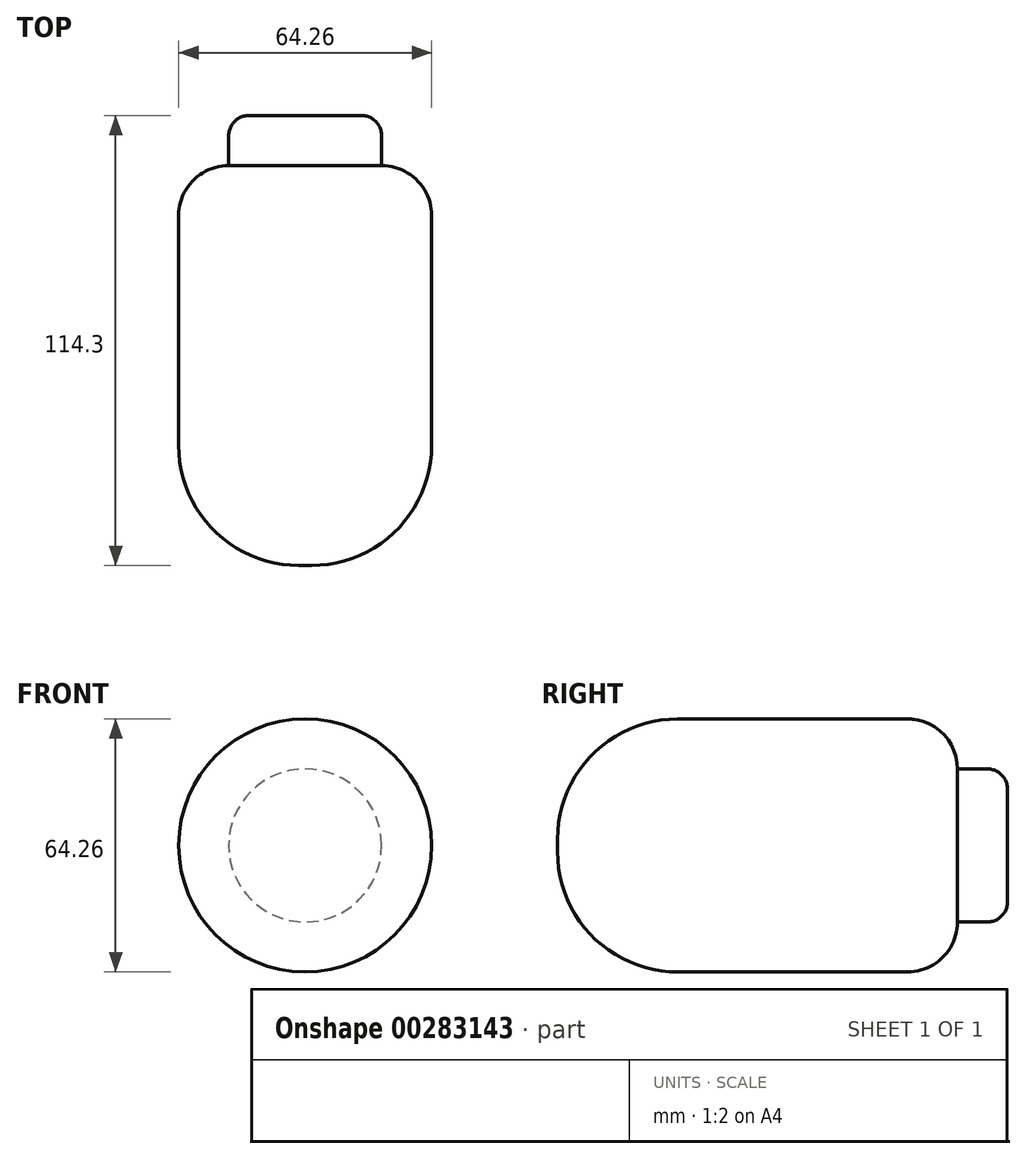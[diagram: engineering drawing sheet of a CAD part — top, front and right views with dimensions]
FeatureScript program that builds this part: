
annotation { "Feature Type Name" : "Feature", "Feature Type Description" : "" }
export const myFeature = defineFeature(function(context is Context, id is Id, definition is map)
    precondition{}
    {
        {
            var Q0;
            Q0=qCreatedBy(makeId("Front.planeOp"),FACE);
            var sketch = newSketch(context, id + "F0", { "sketchPlane" : qUnion([Q0])});
            skCircle(sketch, "E0", {"center": v(0, 0) * mm, "radius": 32.13 * mm});
            skSolve(sketch);
        }
        {
            var Q0;
            Q0=makeQuery(id+"F0.imprint","IMPRINT",FACE,{"disambiguationData":[TD([[makeQuery(id+"F0.imprint","IMPRINT",EDGE,{"derivedFrom":sQuery(id+"F0.wireOp",EDGE,"E0")}),1.0]])]});
            extrude(context, id + "F1", {"entities" : qUnion([Q0]), "endBound" : BoundingType.SYMMETRIC, "depth" : 101.6 * mm});
        }
        {
            var Q0;
            Q0=makeQuery(id+"F1.opExtrude","CAP_FACE",FACE,{"disambiguationData":[OSD([sQuery(id+"F0.wireOp",EDGE,"E0")])],"isStart":false});
            fillet(context, id + "F2", {"entities" : qUnion([Q0]), "radius" : 30.48 * mm, "tangentPropagation" : true, "allowEdgeOverflow" : false});
        }
        {
            var Q0;
            Q0=makeQuery(id+"F1.opExtrude","CAP_FACE",FACE,{"disambiguationData":[OSD([sQuery(id+"F0.wireOp",EDGE,"E0")])],"isStart":true});
            fillet(context, id + "F3", {"entities" : qUnion([Q0]), "radius" : 12.7 * mm, "tangentPropagation" : true, "allowEdgeOverflow" : false});
        }
        {
            var Q0;
            Q0=makeQuery(id+"F1.opExtrude","CAP_FACE",FACE,{"disambiguationData":[OSD([sQuery(id+"F0.wireOp",EDGE,"E0")])],"isStart":true});
            extrude(context, id + "F4", {"entities" : qUnion([Q0]), "operationType" : NewBodyOperationType.ADD, "depth" : 12.7 * mm});
        }
        {
            var Q0;
            Q0=makeQuery(id+"F4.opExtrude","CAP_EDGE",EDGE,{"disambiguationData":[OSD([sQuery(id+"F0.wireOp",EDGE,"E0")])],"isStart":false});
            fillet(context, id + "F5", {"entities" : qUnion([Q0]), "radius" : 5.08 * mm, "tangentPropagation" : true, "allowEdgeOverflow" : false});
        }
    });
